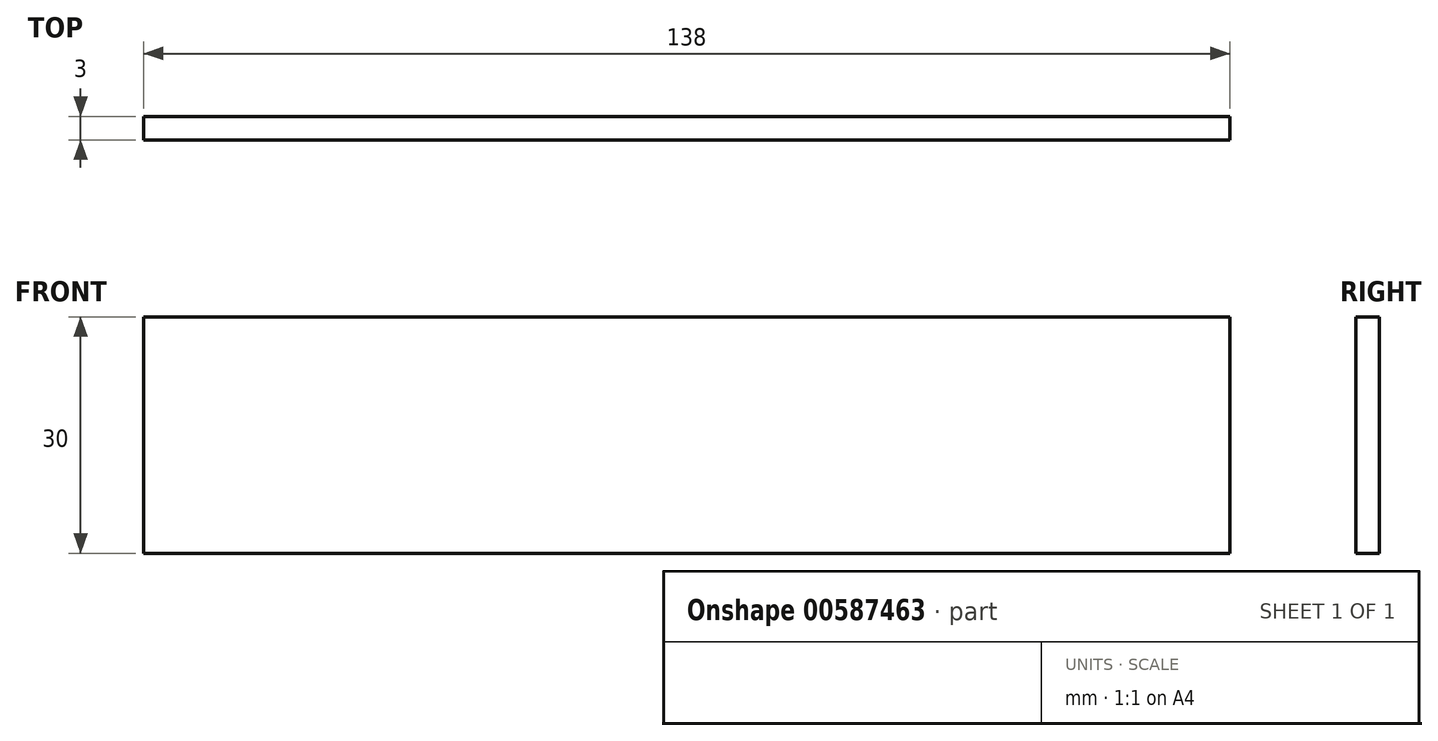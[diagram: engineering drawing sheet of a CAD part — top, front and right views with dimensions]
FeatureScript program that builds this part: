
annotation { "Feature Type Name" : "Feature", "Feature Type Description" : "" }
export const myFeature = defineFeature(function(context is Context, id is Id, definition is map)
    precondition{}
    {
        {
            var Q0;
            Q0=qCreatedBy(makeId("Front.planeOp"),FACE);
            var sketch = newSketch(context, id + "F0", { "sketchPlane" : qUnion([Q0])});
            skLineSegment(sketch, "E0.bottom", {"start": v(-46.3, 29.83) * mm, "end": v(91.7, 29.83) * mm});
            skLineSegment(sketch, "E0.top", {"start": v(-46.3, -0.17) * mm, "end": v(91.7, -0.17) * mm});
            skLineSegment(sketch, "E0.left", {"start": v(-46.3, 29.83) * mm, "end": v(-46.3, -0.17) * mm});
            skLineSegment(sketch, "E0.right", {"start": v(91.7, 29.83) * mm, "end": v(91.7, -0.17) * mm});
            skSolve(sketch);
        }
        {
            var Q0;
            Q0 = qSketchRegion(id + "F0", true);
            extrude(context, id + "F1", {"entities" : qUnion([Q0]), "depth" : 3 * mm, "offsetDistance" : 25 * mm});
        }
    });
